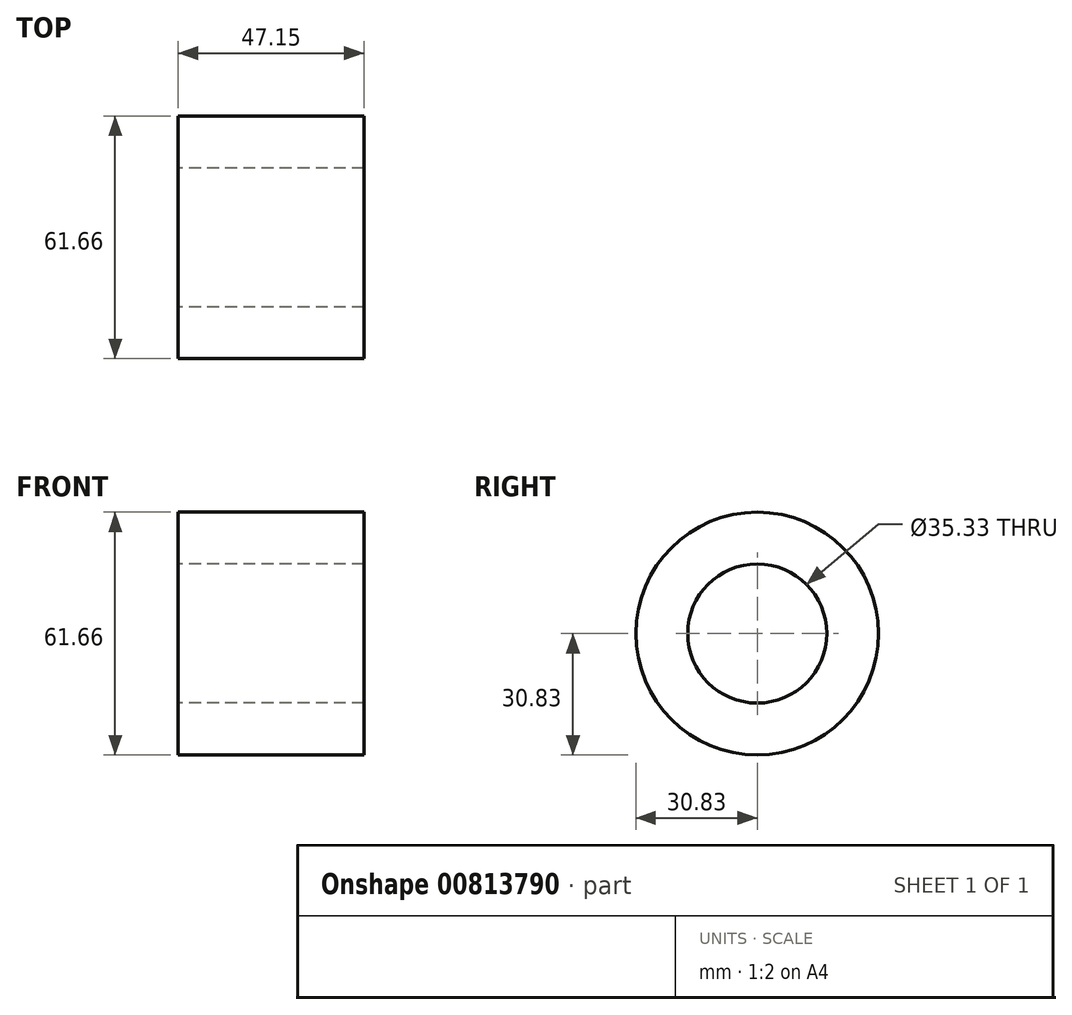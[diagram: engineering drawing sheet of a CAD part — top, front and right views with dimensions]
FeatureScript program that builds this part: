
annotation { "Feature Type Name" : "Feature", "Feature Type Description" : "" }
export const myFeature = defineFeature(function(context is Context, id is Id, definition is map)
    precondition{}
    {
        {
            var Q0;
            Q0=qCreatedBy(makeId("Front.planeOp"),FACE);
            var sketch = newSketch(context, id + "F0", { "sketchPlane" : qUnion([Q0])});
            skLineSegment(sketch, "E0", {"start": v(-21.7, 0) * mm, "end": v(56.43, 0) * mm, "construction": true});
            skLineSegment(sketch, "E1", {"start": v(56.43, 0) * mm, "end": v(68.1, 17.96) * mm, "construction": true});
            skLineSegment(sketch, "E2", {"start": v(0, -17.66) * mm, "end": v(0, -30.83) * mm});
            skLineSegment(sketch, "E3", {"start": v(0, -30.83) * mm, "end": v(47.15, -30.83) * mm});
            skLineSegment(sketch, "E4", {"start": v(47.15, -30.83) * mm, "end": v(47.15, -17.66) * mm});
            skLineSegment(sketch, "E5", {"start": v(0, -17.66) * mm, "end": v(47.15, -17.66) * mm});
            skPoint(sketch, "E6.end.orphan", {"position": v(0, 0) * mm});
            skSolve(sketch);
        }
        {
            var Q0;
            Q0 = qSketchRegion(id + "F0", true);
            var Q1;
            Q1=sQuery(id+"F0.wireOp",EDGE,"E0");
            revolve(context, id + "F1", {"surfaceOperationType" : NewSurfaceOperationType.NEW, "entities" : qUnion([Q0]), "axis" : qUnion([Q1]), "revolveType" : RevolveType.FULL});
        }
    });
